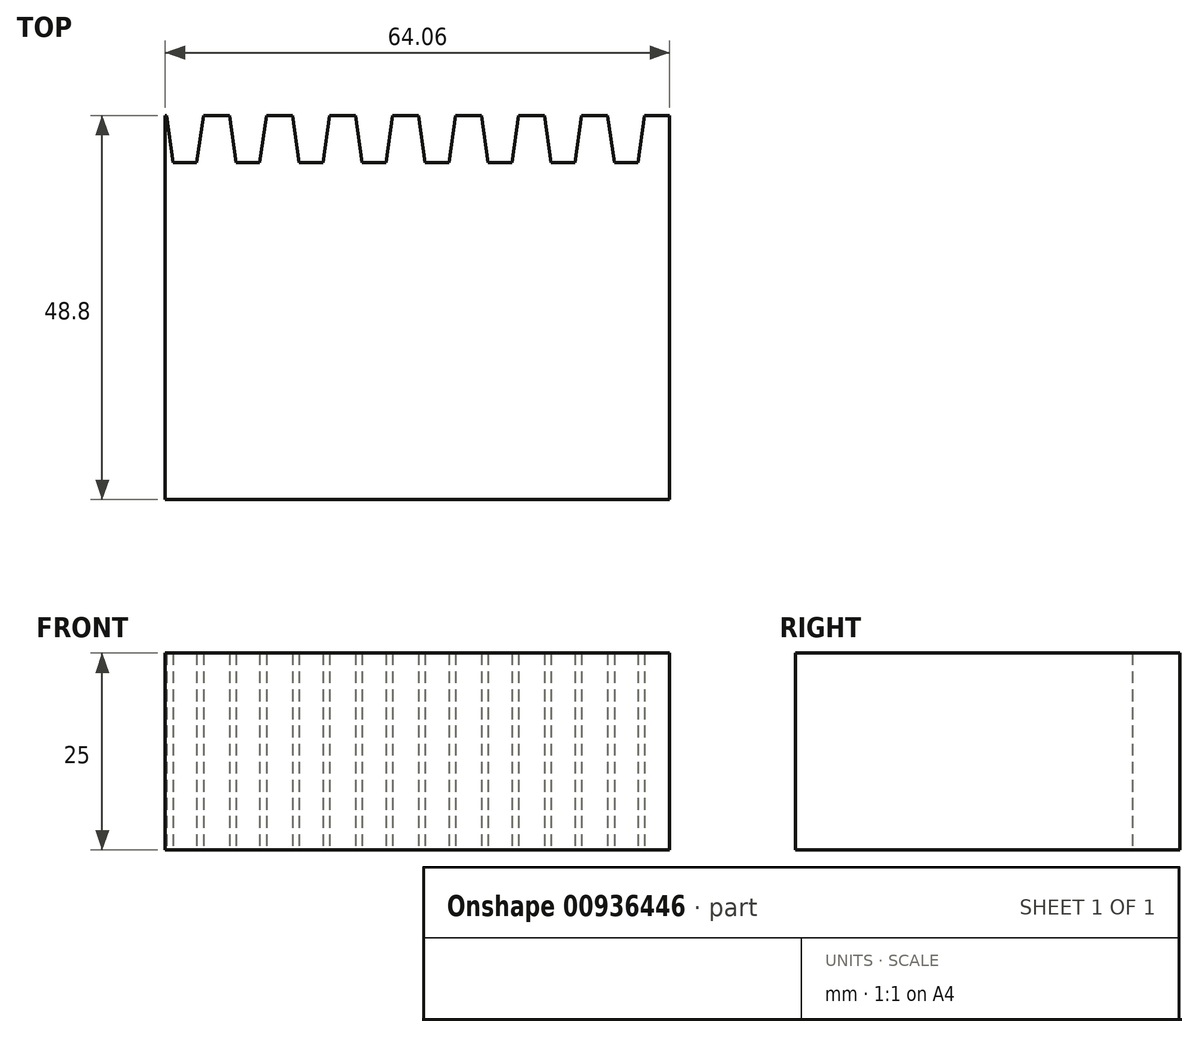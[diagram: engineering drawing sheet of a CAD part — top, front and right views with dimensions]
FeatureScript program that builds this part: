
annotation { "Feature Type Name" : "Feature", "Feature Type Description" : "" }
export const myFeature = defineFeature(function(context is Context, id is Id, definition is map)
    precondition{}
    {
        {
            var Q0;
            Q0=qCreatedBy(makeId("Top.planeOp"),FACE);
            var sketch = newSketch(context, id + "F0", { "sketchPlane" : qUnion([Q0])});
            skLineSegment(sketch, "E0", {"start": v(0, 0) * mm, "end": v(0, -6.88) * mm});
            skLineSegment(sketch, "E1", {"start": v(0.14, -1) * mm, "end": v(0.98, -7) * mm});
            skLineSegment(sketch, "E2", {"start": v(0.98, -7) * mm, "end": v(4, -7) * mm});
            skLineSegment(sketch, "E3", {"start": v(4, -7) * mm, "end": v(4.85, -1) * mm});
            skLineSegment(sketch, "E4", {"start": v(4.99, 0) * mm, "end": v(8, 0) * mm});
            skLineSegment(sketch, "E5.1.0.0", {"start": v(8, 0) * mm, "end": v(9, -7) * mm});
            skLineSegment(sketch, "E5.1.0.1", {"start": v(9, -7) * mm, "end": v(12.01, -7) * mm});
            skLineSegment(sketch, "E5.1.0.2", {"start": v(12.01, -7) * mm, "end": v(12.85, -1) * mm});
            skLineSegment(sketch, "E5.1.0.3", {"start": v(13, 0) * mm, "end": v(16.02, 0) * mm});
            skLineSegment(sketch, "E5.2.0.0", {"start": v(16.02, 0) * mm, "end": v(17, -7) * mm});
            skLineSegment(sketch, "E5.2.0.1", {"start": v(17, -7) * mm, "end": v(20.02, -7) * mm});
            skLineSegment(sketch, "E5.2.0.2", {"start": v(20.02, -7) * mm, "end": v(20.86, -1) * mm});
            skLineSegment(sketch, "E5.2.0.3", {"start": v(21, 0) * mm, "end": v(24.02, 0) * mm});
            skLineSegment(sketch, "E5.3.0.0", {"start": v(24.02, 0) * mm, "end": v(25, -7) * mm});
            skLineSegment(sketch, "E5.3.0.1", {"start": v(25, -7) * mm, "end": v(28.03, -7) * mm});
            skLineSegment(sketch, "E5.3.0.2", {"start": v(28.03, -7) * mm, "end": v(28.87, -1) * mm});
            skLineSegment(sketch, "E5.3.0.3", {"start": v(29.01, 0) * mm, "end": v(32.03, 0) * mm});
            skLineSegment(sketch, "E5.4.0.0", {"start": v(32.03, 0) * mm, "end": v(33.01, -7) * mm});
            skLineSegment(sketch, "E5.4.0.1", {"start": v(33.01, -7) * mm, "end": v(36.03, -7) * mm});
            skLineSegment(sketch, "E5.4.0.2", {"start": v(36.03, -7) * mm, "end": v(36.88, -1) * mm});
            skLineSegment(sketch, "E5.4.0.3", {"start": v(37.02, 0) * mm, "end": v(40.04, 0) * mm});
            skLineSegment(sketch, "E5.5.0.0", {"start": v(40.04, 0) * mm, "end": v(41.02, -7) * mm});
            skLineSegment(sketch, "E5.5.0.1", {"start": v(41.02, -7) * mm, "end": v(44.04, -7) * mm});
            skLineSegment(sketch, "E5.5.0.2", {"start": v(44.04, -7) * mm, "end": v(44.88, -1) * mm});
            skLineSegment(sketch, "E5.5.0.3", {"start": v(45.03, 0) * mm, "end": v(48.05, 0) * mm});
            skLineSegment(sketch, "E5.6.0.0", {"start": v(48.05, 0) * mm, "end": v(49.03, -7) * mm});
            skLineSegment(sketch, "E5.6.0.1", {"start": v(49.03, -7) * mm, "end": v(52.05, -7) * mm});
            skLineSegment(sketch, "E5.6.0.2", {"start": v(52.05, -7) * mm, "end": v(52.9, -1) * mm});
            skLineSegment(sketch, "E5.6.0.3", {"start": v(53.03, 0) * mm, "end": v(56.05, 0) * mm});
            skLineSegment(sketch, "E5.7.0.0", {"start": v(56.2, -1) * mm, "end": v(57.04, -7) * mm});
            skLineSegment(sketch, "E5.7.0.1", {"start": v(57.04, -7) * mm, "end": v(60.06, -7) * mm});
            skLineSegment(sketch, "E5.7.0.2", {"start": v(60.06, -7) * mm, "end": v(60.9, -1) * mm});
            skLineSegment(sketch, "E5.7.0.3", {"start": v(61.04, 0) * mm, "end": v(64.06, 0) * mm});
            skLineSegment(sketch, "E5.direction1", {"start": v(0.98, -7) * mm, "end": v(9, -7) * mm, "construction": true});
            skLineSegment(sketch, "E6", {"start": v(0, 0) * mm, "end": v(0, -49.8) * mm});
            skLineSegment(sketch, "E7", {"start": v(0, -49.8) * mm, "end": v(64.06, -49.8) * mm});
            skLineSegment(sketch, "E8", {"start": v(64.06, -49.8) * mm, "end": v(64.06, 0) * mm});
            skLineSegment(sketch, "E9", {"start": v(0, 0) * mm, "end": v(0, -1) * mm});
            skLineSegment(sketch, "E10", {"start": v(0, -1) * mm, "end": v(0.14, -1) * mm});
            skLineSegment(sketch, "E11.trimOffspring", {"start": v(12.85, -1) * mm, "end": v(16.16, -1) * mm});
            skLineSegment(sketch, "E12.trimOffspring", {"start": v(4.85, -1) * mm, "end": v(8.15, -1) * mm});
            skLineSegment(sketch, "E13.trimOffspring", {"start": v(20.86, -1) * mm, "end": v(24.16, -1) * mm});
            skLineSegment(sketch, "E14.trimOffspring", {"start": v(28.87, -1) * mm, "end": v(32.17, -1) * mm});
            skLineSegment(sketch, "E15.trimOffspring", {"start": v(36.88, -1) * mm, "end": v(40.18, -1) * mm});
            skLineSegment(sketch, "E16.trimOffspring", {"start": v(44.88, -1) * mm, "end": v(48.19, -1) * mm});
            skLineSegment(sketch, "E17.trimOffspring", {"start": v(52.9, -1) * mm, "end": v(56.2, -1) * mm});
            skLineSegment(sketch, "E18.trimOffspring", {"start": v(60.9, -1) * mm, "end": v(64.06, -1) * mm});
            skPoint(sketch, "E19.orphan", {"position": v(56.05, 0) * mm});
            skSolve(sketch);
        }
        {
            var Q0;
            Q0=makeQuery(id+"F0.imprint","IMPRINT",FACE,{"disambiguationData":[TD([[makeQuery(id+"F0.imprint","IMPRINT",EDGE,{"derivedFrom":sQuery(id+"F0.wireOp",EDGE,"E1")}),-1.0]])]});
            extrude(context, id + "F1", {"entities" : qUnion([Q0]), "depth" : 25 * mm, "offsetDistance" : 25 * mm});
        }
    });
